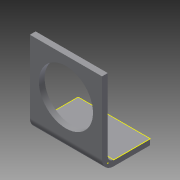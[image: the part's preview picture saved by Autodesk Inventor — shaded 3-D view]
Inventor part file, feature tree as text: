
AUTODESK INVENTOR PART (.ipt)
format: ipt  version: 2013 (Build 170138000, 138)  size: 114,688 bytes
history: native  units: in
note: dims shown in document units (in); Inventor stores cm internally (conversion verified against a paired STEP export)
features: sheet_metal_op x4, sketch x4, other x3
ambient origin geometry x8: Origin, YZ Plane, XZ Plane, XY Plane, X Axis, Y Axis, Z Axis, Center Point
bodies: Solid1 (feature_tree)
feature tree (11):
  sheet_metal_op  "Face1"
  sheet_metal_op  "Flange1"
  sketch  "Sketch5"  dims[d3=0.75in d4=0.12in d7=0.75in d8=1.125in d9=0.12in d10=0.0in d11=0.12in d12=0.06in d13=0.24in d14=0.12in d15=1.0in d16=90.0deg d17=0.12in d18=0.48in d19=0.12in d20=0.12in]
  sketch  "Sketch1"  dims[d0=1.5in]
  other  "Plate1"
  sketch  "Sketch2"  dims[d1=1.5in]
  sketch  "Sketch3"  dims[d2=0.75in]
  other  "Plate2"
  sheet_metal_op  "Bend1"
  sheet_metal_op  "Corner1"
  other  "Cut1"
